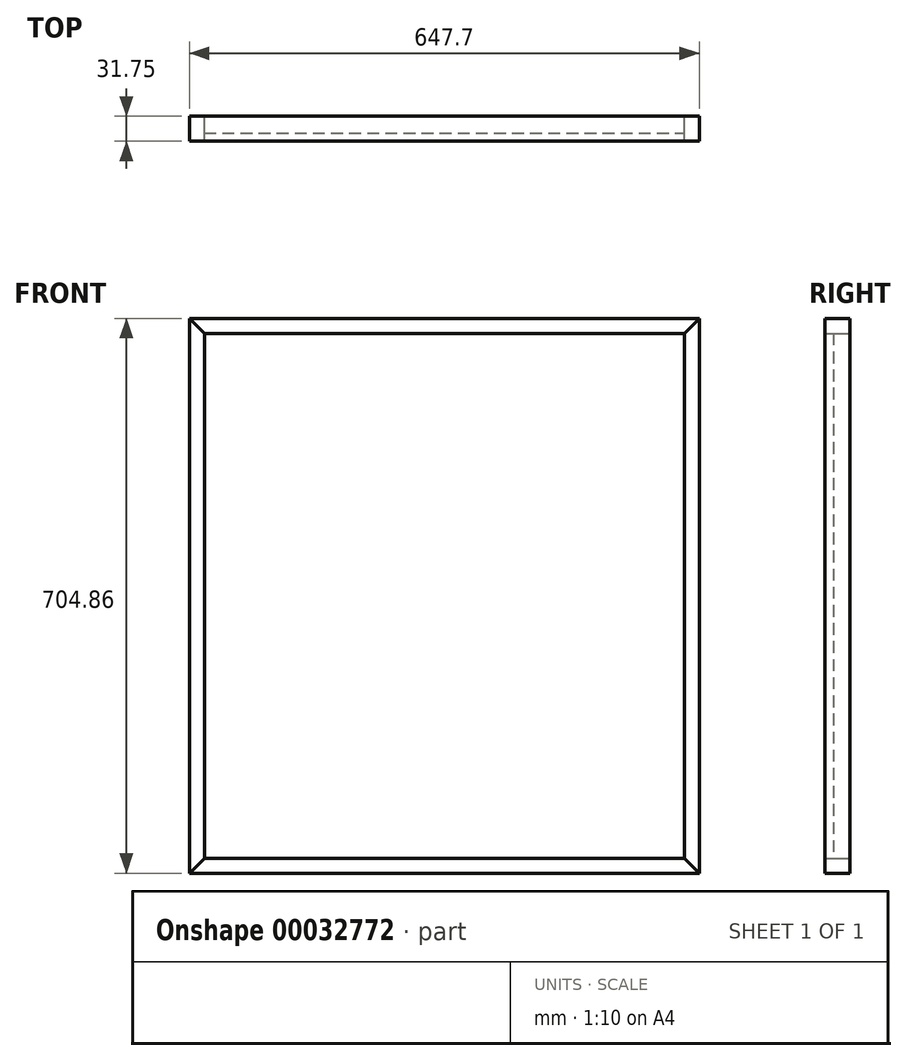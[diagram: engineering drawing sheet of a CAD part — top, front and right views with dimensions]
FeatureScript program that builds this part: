
annotation { "Feature Type Name" : "Feature", "Feature Type Description" : "" }
export const myFeature = defineFeature(function(context is Context, id is Id, definition is map)
    precondition{}
    {
        {
            var Q0;
            Q0=qCreatedBy(makeId("Front.planeOp"),FACE);
            var sketch = newSketch(context, id + "F0", { "sketchPlane" : qUnion([Q0])});
            skLineSegment(sketch, "E0.bottom", {"start": v(-304.8, 333.38) * mm, "end": v(304.8, 333.38) * mm});
            skLineSegment(sketch, "E0.top", {"start": v(-304.8, -333.38) * mm, "end": v(304.8, -333.38) * mm});
            skLineSegment(sketch, "E0.left", {"start": v(-304.8, 333.38) * mm, "end": v(-304.8, -333.38) * mm});
            skLineSegment(sketch, "E0.right", {"start": v(304.8, 333.37) * mm, "end": v(304.8, -333.38) * mm});
            skLineSegment(sketch, "E1", {"start": v(0, 333.38) * mm, "end": v(0, -333.38) * mm, "construction": true});
            skLineSegment(sketch, "E2.bottom", {"start": v(-323.85, 352.43) * mm, "end": v(323.85, 352.43) * mm});
            skLineSegment(sketch, "E2.top", {"start": v(-323.85, -352.43) * mm, "end": v(323.85, -352.43) * mm});
            skLineSegment(sketch, "E2.left", {"start": v(-323.85, 352.43) * mm, "end": v(-323.85, -352.43) * mm});
            skLineSegment(sketch, "E2.right", {"start": v(323.85, 352.43) * mm, "end": v(323.85, -352.43) * mm});
            skLineSegment(sketch, "E3", {"start": v(-323.85, 352.43) * mm, "end": v(-304.8, 333.38) * mm});
            skLineSegment(sketch, "E4", {"start": v(304.8, 333.38) * mm, "end": v(323.85, 352.43) * mm});
            skLineSegment(sketch, "E5", {"start": v(323.85, -352.43) * mm, "end": v(304.8, -333.38) * mm});
            skLineSegment(sketch, "E6", {"start": v(-323.85, -352.43) * mm, "end": v(-304.8, -333.38) * mm});
            skSolve(sketch);
        }
        {
            var Q0;
            Q0=makeQuery(id+"F0.imprint","IMPRINT",FACE,{"disambiguationData":[TD([[makeQuery(id+"F0.imprint","IMPRINT",EDGE,{"derivedFrom":sQuery(id+"F0.wireOp",EDGE,"E0.bottom")}),-1.0]])]});
            extrude(context, id + "F1", {"entities" : qUnion([Q0]), "depth" : 21.43 * mm});
        }
        {
            var Q0;
            Q0=makeQuery(id+"F0.imprint","IMPRINT",FACE,{"disambiguationData":[TD([[makeQuery(id+"F0.imprint","IMPRINT",EDGE,{"derivedFrom":sQuery(id+"F0.wireOp",EDGE,"E0.bottom")}),1.0]])]});
            extrude(context, id + "F2", {"entities" : qUnion([Q0]), "depth" : 31.75 * mm});
        }
        {
            var Q0;
            Q0=makeQuery(id+"F0.imprint","IMPRINT",FACE,{"disambiguationData":[TD([[makeQuery(id+"F0.imprint","IMPRINT",EDGE,{"derivedFrom":sQuery(id+"F0.wireOp",EDGE,"E0.left")}),-1.0]])]});
            extrude(context, id + "F3", {"entities" : qUnion([Q0]), "depth" : 31.75 * mm});
        }
        {
            var Q0;
            Q0=makeQuery(id+"F0.imprint","IMPRINT",FACE,{"disambiguationData":[TD([[makeQuery(id+"F0.imprint","IMPRINT",EDGE,{"derivedFrom":sQuery(id+"F0.wireOp",EDGE,"E0.top")}),-1.0]])]});
            extrude(context, id + "F4", {"entities" : qUnion([Q0]), "depth" : 31.75 * mm});
        }
        {
            var Q0;
            Q0=makeQuery(id+"F0.imprint","IMPRINT",FACE,{"disambiguationData":[TD([[makeQuery(id+"F0.imprint","IMPRINT",EDGE,{"derivedFrom":sQuery(id+"F0.wireOp",EDGE,"E0.right")}),1.0]])]});
            extrude(context, id + "F5", {"entities" : qUnion([Q0]), "depth" : 31.75 * mm});
        }
    });
